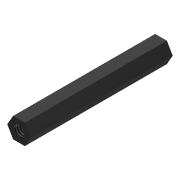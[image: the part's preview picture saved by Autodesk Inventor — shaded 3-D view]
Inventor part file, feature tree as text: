
AUTODESK INVENTOR PART (.ipt)
format: ipt  version: 2013 (Build 170138000, 138)  size: 84,480 bytes
history: native  units: in
note: dims shown in document units (in); Inventor stores cm internally (conversion verified against a paired STEP export)
features: sketch x2, extrude x1, hole x1, mirror x1
ambient origin geometry x8: Origin, YZ Plane, XZ Plane, XY Plane, X Axis, Y Axis, Z Axis, Center Point
bodies: Solid1 (feature_tree)
feature tree (5):
  extrude  "Extrusion1"  Depth=1.75in TaperAngle=0.0deg
  hole  "Hole1"  [1 undecoded]
  mirror  "Mirror1"
  sketch  "Sketch1"  dims[d0=0.25in d1=1.75in d2=0.0in]
  sketch  "Sketch2"  dims[d3=0.13in d4=0.375in d5=0.375in d6=0.25in d7=0.5635in d8=0.375in d9=0.0in]
note: 1 required parameter value undecoded (feature->parameter linkage not recoverable at this tier; creation-order binding heuristic only, values carry confidence <= 0.55)
